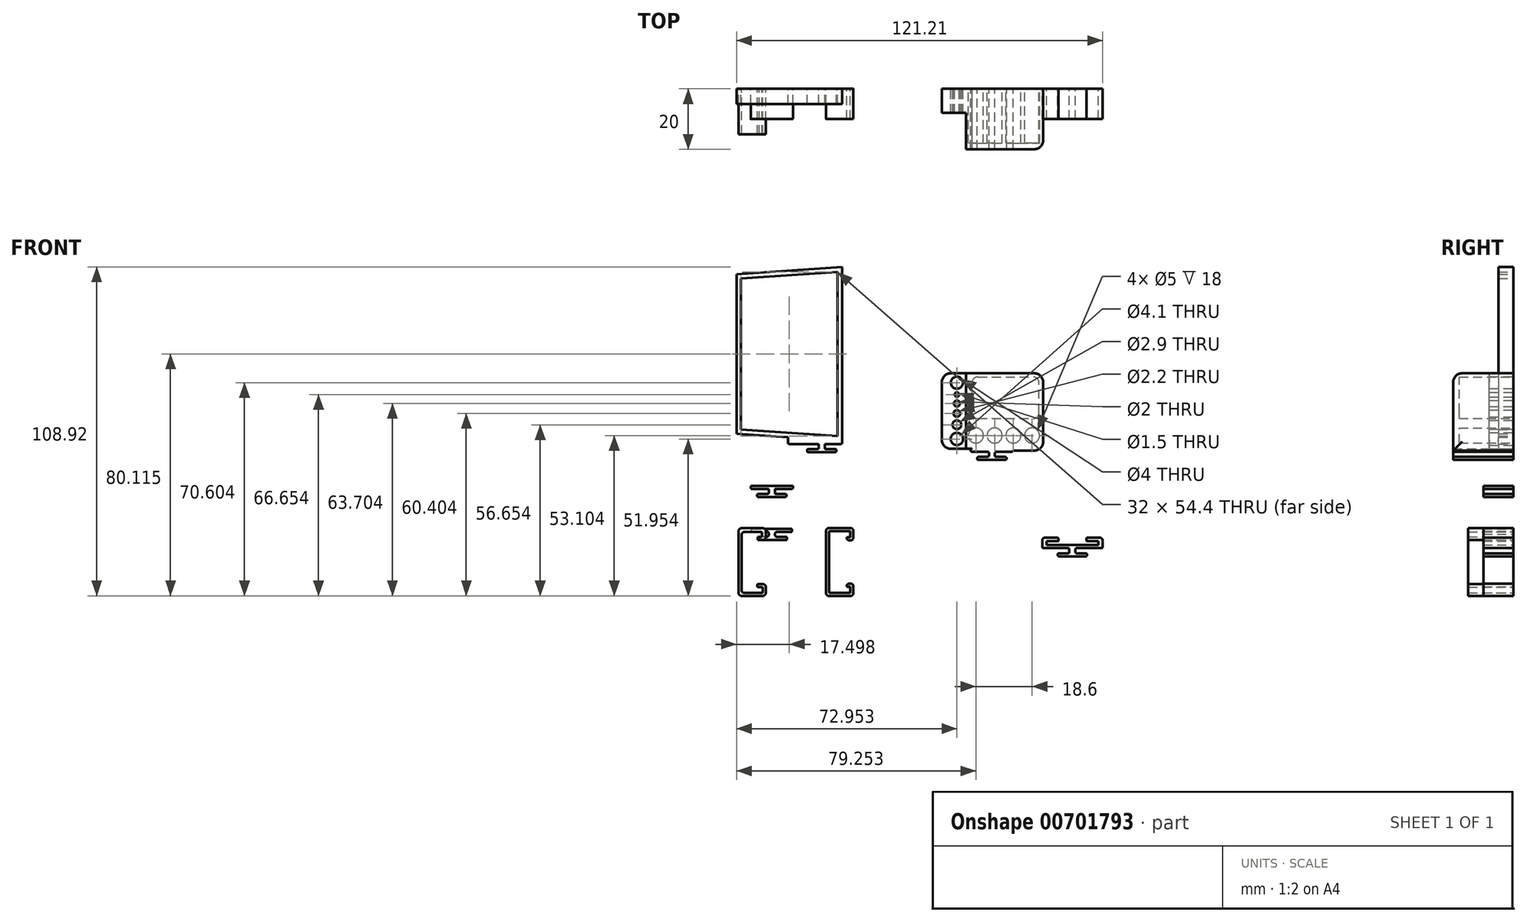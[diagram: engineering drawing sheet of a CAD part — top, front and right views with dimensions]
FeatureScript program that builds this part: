
annotation { "Feature Type Name" : "Feature", "Feature Type Description" : "" }
export const myFeature = defineFeature(function(context is Context, id is Id, definition is map)
    precondition{}
    {
        {
            var Q0;
            Q0=qCreatedBy(makeId("Front.planeOp"),FACE);
            var sketch = newSketch(context, id + "F0", { "sketchPlane" : qUnion([Q0])});
            skLineSegment(sketch, "E0.bottom", {"start": v(-9, 10) * mm, "end": v(-3.2, 10) * mm});
            skLineSegment(sketch, "E0.top", {"start": v(-9, -10) * mm, "end": v(-3.2, -10) * mm});
            skLineSegment(sketch, "E0.left", {"start": v(-10, 9) * mm, "end": v(-10, -9) * mm});
            skLineSegment(sketch, "E0.right", {"start": v(10, 9) * mm, "end": v(10, -9) * mm});
            skLineSegment(sketch, "E1.bottom", {"start": v(-3, 3) * mm, "end": v(3, 3) * mm});
            skLineSegment(sketch, "E1.top", {"start": v(-3, -3) * mm, "end": v(3, -3) * mm});
            skLineSegment(sketch, "E1.left", {"start": v(-3, 3) * mm, "end": v(-3, -3) * mm});
            skLineSegment(sketch, "E1.right", {"start": v(3, 3) * mm, "end": v(3, -3) * mm});
            skLineSegment(sketch, "E2", {"start": v(-3.2, 10) * mm, "end": v(-3.2, 8) * mm});
            skLineSegment(sketch, "E3", {"start": v(-3.2, 8) * mm, "end": v(-5.25, 8) * mm});
            skLineSegment(sketch, "E4", {"start": v(-5.25, 8) * mm, "end": v(-5.25, 6.5) * mm});
            skLineSegment(sketch, "E5", {"start": v(-5.25, 6.5) * mm, "end": v(-2.23, 3) * mm});
            skLineSegment(sketch, "E6", {"start": v(-3.2, -10) * mm, "end": v(-3.2, -8) * mm});
            skLineSegment(sketch, "E7", {"start": v(-3.2, -8) * mm, "end": v(-5.25, -8) * mm});
            skLineSegment(sketch, "E8", {"start": v(-5.25, -8) * mm, "end": v(-5.25, -6.5) * mm});
            skLineSegment(sketch, "E9", {"start": v(-5.25, -6.5) * mm, "end": v(-2.23, -3) * mm});
            skPoint(sketch, "E10.visualSharp", {"position": v(-10, 10) * mm});
            skArc(sketch, "E10.filletArc", {"start": v(-9, 10) * mm, "mid": v(-9.7, 9.7) * mm, "end": v(-10, 9) * mm});
            skPoint(sketch, "E11.visualSharp", {"position": v(-10, -10) * mm});
            skArc(sketch, "E11.filletArc", {"start": v(-10, -9) * mm, "mid": v(-9.7, -9.7) * mm, "end": v(-9, -10) * mm});
            skPoint(sketch, "E12.visualSharp", {"position": v(10, -10) * mm});
            skArc(sketch, "E12.filletArc", {"start": v(9, -10) * mm, "mid": v(9.7, -9.7) * mm, "end": v(10, -9) * mm});
            skPoint(sketch, "E13.visualSharp", {"position": v(10, 10) * mm});
            skArc(sketch, "E13.filletArc", {"start": v(10, 9) * mm, "mid": v(9.7, 9.7) * mm, "end": v(9, 10) * mm});
            skLineSegment(sketch, "E14", {"start": v(-4.2, 8.3) * mm, "end": v(-3.3, 8.3) * mm});
            skLineSegment(sketch, "E15", {"start": v(-3, 8.6) * mm, "end": v(-3, 9.9) * mm});
            skLineSegment(sketch, "E16", {"start": v(-3.3, 10.2) * mm, "end": v(-9.2, 10.2) * mm});
            skLineSegment(sketch, "E17", {"start": v(-10, 9.4) * mm, "end": v(-10, -9.4) * mm});
            skLineSegment(sketch, "E18", {"start": v(-9.2, -10.2) * mm, "end": v(-3.3, -10.2) * mm});
            skLineSegment(sketch, "E19", {"start": v(-3, -9.9) * mm, "end": v(-3, -8.6) * mm});
            skLineSegment(sketch, "E20", {"start": v(-3.3, -8.3) * mm, "end": v(-4.74, -8.3) * mm});
            skLineSegment(sketch, "E21", {"start": v(-4.74, -8.3) * mm, "end": v(-4.74, -7.6) * mm});
            skLineSegment(sketch, "E22", {"start": v(-4.44, -7.3) * mm, "end": v(-3, -7.3) * mm});
            skLineSegment(sketch, "E23", {"start": v(-2, -8.3) * mm, "end": v(-2, -10.2) * mm});
            skLineSegment(sketch, "E24", {"start": v(-3, -11.2) * mm, "end": v(-10, -11.2) * mm});
            skLineSegment(sketch, "E25", {"start": v(-11, -10.2) * mm, "end": v(-11, 10.2) * mm});
            skLineSegment(sketch, "E26", {"start": v(-10, 11.2) * mm, "end": v(-3, 11.2) * mm});
            skLineSegment(sketch, "E27", {"start": v(-2, 10.2) * mm, "end": v(-2, 8.3) * mm});
            skLineSegment(sketch, "E28", {"start": v(-3, 7.3) * mm, "end": v(-3.9, 7.3) * mm});
            skLineSegment(sketch, "E29", {"start": v(-4.2, 7.6) * mm, "end": v(-4.2, 8.3) * mm});
            skLineSegment(sketch, "E30.trimOffspring", {"start": v(-2, -10) * mm, "end": v(9, -10) * mm});
            skPoint(sketch, "E31.visualSharp", {"position": v(-11, -11.2) * mm});
            skArc(sketch, "E31.filletArc", {"start": v(-11, -10.2) * mm, "mid": v(-10.7, -10.9) * mm, "end": v(-10, -11.2) * mm});
            skPoint(sketch, "E32.visualSharp", {"position": v(-2, -11.2) * mm});
            skArc(sketch, "E32.filletArc", {"start": v(-3, -11.2) * mm, "mid": v(-2.3, -10.9) * mm, "end": v(-2, -10.2) * mm});
            skPoint(sketch, "E33.visualSharp", {"position": v(-11, 11.2) * mm});
            skArc(sketch, "E33.filletArc", {"start": v(-10, 11.2) * mm, "mid": v(-10.7, 10.9) * mm, "end": v(-11, 10.2) * mm});
            skPoint(sketch, "E34.visualSharp", {"position": v(-2, 11.2) * mm});
            skArc(sketch, "E34.filletArc", {"start": v(-2, 10.2) * mm, "mid": v(-2.3, 10.9) * mm, "end": v(-3, 11.2) * mm});
            skPoint(sketch, "E35.visualSharp", {"position": v(-2, -7.3) * mm});
            skArc(sketch, "E35.filletArc", {"start": v(-2, -8.3) * mm, "mid": v(-2.3, -7.6) * mm, "end": v(-3, -7.3) * mm});
            skPoint(sketch, "E36.visualSharp", {"position": v(-2, 7.3) * mm});
            skArc(sketch, "E36.filletArc", {"start": v(-3, 7.3) * mm, "mid": v(-2.3, 7.6) * mm, "end": v(-2, 8.3) * mm});
            skPoint(sketch, "E37.visualSharp", {"position": v(-4.2, 7.3) * mm});
            skArc(sketch, "E37.filletArc", {"start": v(-4.2, 7.6) * mm, "mid": v(-4.11, 7.39) * mm, "end": v(-3.9, 7.3) * mm});
            skPoint(sketch, "E38.visualSharp", {"position": v(-4.74, -7.3) * mm});
            skArc(sketch, "E38.filletArc", {"start": v(-4.44, -7.3) * mm, "mid": v(-4.65, -7.39) * mm, "end": v(-4.74, -7.6) * mm});
            skArc(sketch, "E39.filletArc", {"start": v(-3.3, 8.3) * mm, "mid": v(-3.09, 8.39) * mm, "end": v(-3, 8.6) * mm});
            skArc(sketch, "E40.filletArc", {"start": v(-3, 9.9) * mm, "mid": v(-3.09, 10.11) * mm, "end": v(-3.3, 10.2) * mm});
            skArc(sketch, "E41.filletArc", {"start": v(-3, -8.6) * mm, "mid": v(-3.09, -8.39) * mm, "end": v(-3.3, -8.3) * mm});
            skArc(sketch, "E42.filletArc", {"start": v(-3.3, -10.2) * mm, "mid": v(-3.09, -10.11) * mm, "end": v(-3, -9.9) * mm});
            skArc(sketch, "E43.filletArc", {"start": v(-10, -9.4) * mm, "mid": v(-9.77, -9.97) * mm, "end": v(-9.2, -10.2) * mm});
            skArc(sketch, "E44.filletArc", {"start": v(-9.2, 10.2) * mm, "mid": v(-9.77, 9.97) * mm, "end": v(-10, 9.4) * mm});
            skLineSegment(sketch, "E45", {"start": v(3.2, 10) * mm, "end": v(3.2, 8) * mm});
            skLineSegment(sketch, "E46", {"start": v(3.2, 8) * mm, "end": v(5.25, 8) * mm});
            skLineSegment(sketch, "E47", {"start": v(5.25, 8) * mm, "end": v(5.25, 6.5) * mm});
            skLineSegment(sketch, "E48", {"start": v(5.25, 6.5) * mm, "end": v(2.23, 3) * mm});
            skLineSegment(sketch, "E49.bottom", {"start": v(1.8, 8.3) * mm, "end": v(4.5, 8.3) * mm});
            skLineSegment(sketch, "E49.top", {"start": v(-3.2, 7.3) * mm, "end": v(5.3, 7.3) * mm});
            skLineSegment(sketch, "E49.left", {"start": v(-3.2, 8.8) * mm, "end": v(-3.2, 7.3) * mm});
            skLineSegment(sketch, "E50.top", {"start": v(-4.64, 11) * mm, "end": v(4.5, 11) * mm});
            skLineSegment(sketch, "E51.top", {"start": v(-0.8, 8.3) * mm, "end": v(1, 8.3) * mm});
            skArc(sketch, "E52.filletArc", {"start": v(1, 9.15) * mm, "mid": v(1.22, 8.55) * mm, "end": v(1.8, 8.3) * mm});
            skLineSegment(sketch, "E53", {"start": v(-1.8, 8.3) * mm, "end": v(-4.2, 8.3) * mm});
            skPoint(sketch, "E54.visualSharp", {"position": v(-0.8, 8.3) * mm});
            skArc(sketch, "E54.filletArc", {"start": v(-1.8, 8.3) * mm, "mid": v(-1.22, 8.55) * mm, "end": v(-1, 9.15) * mm});
            skPoint(sketch, "E55.visualSharp", {"position": v(-0.8, 10.05) * mm});
            skLineSegment(sketch, "E56.bottom", {"start": v(-4.2, 8.3) * mm, "end": v(-4.7, 8.3) * mm});
            skLineSegment(sketch, "E56.top", {"start": v(-4.2, 7.3) * mm, "end": v(-4.7, 7.3) * mm});
            skLineSegment(sketch, "E56.left", {"start": v(-4.2, 8) * mm, "end": v(-4.2, 7.3) * mm});
            skLineSegment(sketch, "E56.right", {"start": v(-4.7, 8.3) * mm, "end": v(-4.7, 7.3) * mm});
            skLineSegment(sketch, "E57", {"start": v(-3.2, 7.3) * mm, "end": v(-4.7, 7.3) * mm});
            skLineSegment(sketch, "E58", {"start": v(-4.7, 7.3) * mm, "end": v(-2, 7.3) * mm});
            skLineSegment(sketch, "E59.bottom", {"start": v(4.5, 8.3) * mm, "end": v(5, 8.3) * mm});
            skLineSegment(sketch, "E59.top", {"start": v(5, 7.3) * mm, "end": v(5.3, 7.3) * mm});
            skLineSegment(sketch, "E59.right", {"start": v(5, 8.3) * mm, "end": v(5, 7.3) * mm});
            skLineSegment(sketch, "E60.right", {"start": v(6.64, 10) * mm, "end": v(6.64, 11) * mm});
            skLineSegment(sketch, "E61.bottom", {"start": v(-4.64, 11) * mm, "end": v(-6.64, 11) * mm});
            skLineSegment(sketch, "E61.top", {"start": v(-4.5, 10.2) * mm, "end": v(-6.64, 10.2) * mm});
            skLineSegment(sketch, "E61.right", {"start": v(-6.64, 10.2) * mm, "end": v(-6.64, 11) * mm});
            skLineSegment(sketch, "E62", {"start": v(-1, 9.15) * mm, "end": v(-1, 9.15) * mm});
            skLineSegment(sketch, "E63", {"start": v(4.5, 11) * mm, "end": v(6.64, 11) * mm});
            skLineSegment(sketch, "E64", {"start": v(1, 9.15) * mm, "end": v(1, 9.2) * mm});
            skLineSegment(sketch, "E65", {"start": v(1.8, 10) * mm, "end": v(6.64, 10) * mm});
            skLineSegment(sketch, "E66", {"start": v(6.64, 10) * mm, "end": v(9, 10) * mm});
            skPoint(sketch, "E67.visualSharp", {"position": v(1, 10) * mm});
            skArc(sketch, "E67.filletArc", {"start": v(1.8, 10) * mm, "mid": v(1.23, 9.77) * mm, "end": v(1, 9.2) * mm});
            skLineSegment(sketch, "E68", {"start": v(-3.3, 10.2) * mm, "end": v(-1.8, 10.2) * mm});
            skLineSegment(sketch, "E69", {"start": v(-1, 9.4) * mm, "end": v(-1, 9.15) * mm});
            skPoint(sketch, "E70.visualSharp", {"position": v(-1, 10.2) * mm});
            skArc(sketch, "E70.filletArc", {"start": v(-1, 9.4) * mm, "mid": v(-1.23, 9.97) * mm, "end": v(-1.8, 10.2) * mm});
            skLineSegment(sketch, "E71", {"start": v(24.8, 8.2) * mm, "end": v(24.8, 8) * mm});
            skLineSegment(sketch, "E72", {"start": v(25.6, 7.2) * mm, "end": v(26.2, 7.2) * mm});
            skLineSegment(sketch, "E73", {"start": v(27, 8) * mm, "end": v(27, 10.4) * mm});
            skLineSegment(sketch, "E74", {"start": v(26.2, 11.2) * mm, "end": v(18.8, 11.2) * mm});
            skLineSegment(sketch, "E75", {"start": v(18, 10.4) * mm, "end": v(18, -10.4) * mm});
            skLineSegment(sketch, "E76", {"start": v(18.8, -11.2) * mm, "end": v(26.2, -11.2) * mm});
            skLineSegment(sketch, "E77", {"start": v(27, -10.4) * mm, "end": v(27, -8) * mm});
            skLineSegment(sketch, "E78", {"start": v(26.2, -7.2) * mm, "end": v(25.6, -7.2) * mm});
            skLineSegment(sketch, "E79", {"start": v(24.8, -8) * mm, "end": v(24.8, -8.2) * mm});
            skLineSegment(sketch, "E80", {"start": v(24.8, -8.2) * mm, "end": v(25.8, -8.2) * mm});
            skLineSegment(sketch, "E81", {"start": v(26, -8.4) * mm, "end": v(26, -10) * mm});
            skLineSegment(sketch, "E82", {"start": v(25.8, -10.2) * mm, "end": v(19.2, -10.2) * mm});
            skLineSegment(sketch, "E83", {"start": v(19, -10) * mm, "end": v(19, 10) * mm});
            skLineSegment(sketch, "E84", {"start": v(19.2, 10.2) * mm, "end": v(25.8, 10.2) * mm});
            skLineSegment(sketch, "E85", {"start": v(26, 10) * mm, "end": v(26, 8.4) * mm});
            skLineSegment(sketch, "E86", {"start": v(25.8, 8.2) * mm, "end": v(24.8, 8.2) * mm});
            skPoint(sketch, "E87.visualSharp", {"position": v(18, 11.2) * mm});
            skArc(sketch, "E87.filletArc", {"start": v(18.8, 11.2) * mm, "mid": v(18.23, 10.97) * mm, "end": v(18, 10.4) * mm});
            skPoint(sketch, "E88.visualSharp", {"position": v(27, 11.2) * mm});
            skArc(sketch, "E88.filletArc", {"start": v(27, 10.4) * mm, "mid": v(26.77, 10.97) * mm, "end": v(26.2, 11.2) * mm});
            skPoint(sketch, "E89.visualSharp", {"position": v(27, 7.2) * mm});
            skArc(sketch, "E89.filletArc", {"start": v(26.2, 7.2) * mm, "mid": v(26.77, 7.43) * mm, "end": v(27, 8) * mm});
            skPoint(sketch, "E90.visualSharp", {"position": v(24.8, 7.2) * mm});
            skArc(sketch, "E90.filletArc", {"start": v(24.8, 8) * mm, "mid": v(25.03, 7.43) * mm, "end": v(25.6, 7.2) * mm});
            skPoint(sketch, "E91.visualSharp", {"position": v(24.8, -7.2) * mm});
            skArc(sketch, "E91.filletArc", {"start": v(25.6, -7.2) * mm, "mid": v(25.03, -7.43) * mm, "end": v(24.8, -8) * mm});
            skPoint(sketch, "E92.visualSharp", {"position": v(27, -7.2) * mm});
            skArc(sketch, "E92.filletArc", {"start": v(27, -8) * mm, "mid": v(26.77, -7.43) * mm, "end": v(26.2, -7.2) * mm});
            skPoint(sketch, "E93.visualSharp", {"position": v(27, -11.2) * mm});
            skArc(sketch, "E93.filletArc", {"start": v(26.2, -11.2) * mm, "mid": v(26.77, -10.97) * mm, "end": v(27, -10.4) * mm});
            skPoint(sketch, "E94.visualSharp", {"position": v(18, -11.2) * mm});
            skArc(sketch, "E94.filletArc", {"start": v(18, -10.4) * mm, "mid": v(18.23, -10.97) * mm, "end": v(18.8, -11.2) * mm});
            skPoint(sketch, "E95.visualSharp", {"position": v(19, -10.2) * mm});
            skArc(sketch, "E95.filletArc", {"start": v(19, -10) * mm, "mid": v(19.06, -10.14) * mm, "end": v(19.2, -10.2) * mm});
            skPoint(sketch, "E96.visualSharp", {"position": v(26, -10.2) * mm});
            skArc(sketch, "E96.filletArc", {"start": v(25.8, -10.2) * mm, "mid": v(25.94, -10.14) * mm, "end": v(26, -10) * mm});
            skPoint(sketch, "E97.visualSharp", {"position": v(26, -8.2) * mm});
            skArc(sketch, "E97.filletArc", {"start": v(26, -8.4) * mm, "mid": v(25.94, -8.26) * mm, "end": v(25.8, -8.2) * mm});
            skPoint(sketch, "E98.visualSharp", {"position": v(19, 10.2) * mm});
            skArc(sketch, "E98.filletArc", {"start": v(19.2, 10.2) * mm, "mid": v(19.06, 10.14) * mm, "end": v(19, 10) * mm});
            skPoint(sketch, "E99.visualSharp", {"position": v(26, 10.2) * mm});
            skArc(sketch, "E99.filletArc", {"start": v(26, 10) * mm, "mid": v(25.94, 10.14) * mm, "end": v(25.8, 10.2) * mm});
            skPoint(sketch, "E100.visualSharp", {"position": v(26, 8.2) * mm});
            skArc(sketch, "E100.filletArc", {"start": v(25.8, 8.2) * mm, "mid": v(25.94, 8.26) * mm, "end": v(26, 8.4) * mm});
            skLineSegment(sketch, "E101", {"start": v(-6.6, 25.24) * mm, "end": v(7, 25.24) * mm});
            skLineSegment(sketch, "E102", {"start": v(7, 25.24) * mm, "end": v(7, 24.64) * mm});
            skLineSegment(sketch, "E103", {"start": v(6.6, 24.24) * mm, "end": v(1.4, 24.24) * mm});
            skLineSegment(sketch, "E104", {"start": v(1, 23.84) * mm, "end": v(1, 22.94) * mm});
            skLineSegment(sketch, "E105", {"start": v(1.4, 22.54) * mm, "end": v(4.45, 22.54) * mm});
            skLineSegment(sketch, "E106", {"start": v(4.85, 22.14) * mm, "end": v(4.85, 21.94) * mm});
            skLineSegment(sketch, "E107", {"start": v(4.45, 21.54) * mm, "end": v(-4.45, 21.54) * mm});
            skLineSegment(sketch, "E108", {"start": v(-4.85, 21.94) * mm, "end": v(-4.85, 22.14) * mm});
            skLineSegment(sketch, "E109", {"start": v(-4.45, 22.54) * mm, "end": v(-1.4, 22.54) * mm});
            skLineSegment(sketch, "E110", {"start": v(-1, 22.94) * mm, "end": v(-1, 23.84) * mm});
            skLineSegment(sketch, "E111", {"start": v(-1.4, 24.24) * mm, "end": v(-6.6, 24.24) * mm});
            skLineSegment(sketch, "E112", {"start": v(-7, 24.64) * mm, "end": v(-7, 24.84) * mm});
            skPoint(sketch, "E113.visualSharp", {"position": v(-1, 22.54) * mm});
            skArc(sketch, "E113.filletArc", {"start": v(-1.4, 22.54) * mm, "mid": v(-1.12, 22.66) * mm, "end": v(-1, 22.94) * mm});
            skPoint(sketch, "E114.visualSharp", {"position": v(1, 22.54) * mm});
            skArc(sketch, "E114.filletArc", {"start": v(1, 22.94) * mm, "mid": v(1.12, 22.66) * mm, "end": v(1.4, 22.54) * mm});
            skPoint(sketch, "E115.visualSharp", {"position": v(1, 24.24) * mm});
            skArc(sketch, "E115.filletArc", {"start": v(1.4, 24.24) * mm, "mid": v(1.12, 24.13) * mm, "end": v(1, 23.84) * mm});
            skPoint(sketch, "E116.visualSharp", {"position": v(-1, 24.24) * mm});
            skArc(sketch, "E116.filletArc", {"start": v(-1, 23.84) * mm, "mid": v(-1.12, 24.13) * mm, "end": v(-1.4, 24.24) * mm});
            skPoint(sketch, "E117.visualSharp", {"position": v(-4.85, 22.54) * mm});
            skArc(sketch, "E117.filletArc", {"start": v(-4.45, 22.54) * mm, "mid": v(-4.73, 22.43) * mm, "end": v(-4.85, 22.14) * mm});
            skPoint(sketch, "E118.visualSharp", {"position": v(-4.85, 21.54) * mm});
            skArc(sketch, "E118.filletArc", {"start": v(-4.85, 21.94) * mm, "mid": v(-4.73, 21.66) * mm, "end": v(-4.45, 21.54) * mm});
            skPoint(sketch, "E119.visualSharp", {"position": v(4.85, 21.54) * mm});
            skArc(sketch, "E119.filletArc", {"start": v(4.45, 21.54) * mm, "mid": v(4.73, 21.66) * mm, "end": v(4.85, 21.94) * mm});
            skPoint(sketch, "E120.visualSharp", {"position": v(4.85, 22.54) * mm});
            skArc(sketch, "E120.filletArc", {"start": v(4.85, 22.14) * mm, "mid": v(4.73, 22.43) * mm, "end": v(4.45, 22.54) * mm});
            skPoint(sketch, "E121.visualSharp", {"position": v(7, 24.24) * mm});
            skArc(sketch, "E121.filletArc", {"start": v(6.6, 24.24) * mm, "mid": v(6.88, 24.36) * mm, "end": v(7, 24.64) * mm});
            skPoint(sketch, "E122.visualSharp", {"position": v(-7, 25.24) * mm});
            skArc(sketch, "E122.filletArc", {"start": v(-6.6, 25.24) * mm, "mid": v(-6.88, 25.13) * mm, "end": v(-7, 24.84) * mm});
            skPoint(sketch, "E123.visualSharp", {"position": v(-7, 24.24) * mm});
            skArc(sketch, "E123.filletArc", {"start": v(-7, 24.64) * mm, "mid": v(-6.88, 24.36) * mm, "end": v(-6.6, 24.24) * mm});
            skLineSegment(sketch, "E124", {"start": v(21.82, 96.11) * mm, "end": v(21.82, 41.71) * mm});
            skLineSegment(sketch, "E125", {"start": v(21.82, 96.11) * mm, "end": v(-10.18, 93.96) * mm});
            skLineSegment(sketch, "E126", {"start": v(-10.18, 93.96) * mm, "end": v(-10.18, 43.86) * mm});
            skLineSegment(sketch, "E127", {"start": v(-10.18, 43.86) * mm, "end": v(21.82, 41.71) * mm});
            skLineSegment(sketch, "E128", {"start": v(13.05, 68.91) * mm, "end": v(-2.86, 68.91) * mm, "construction": true});
            skPoint(sketch, "E128.startSnap0", {"position": v(21.82, 68.91) * mm});
            skLineSegment(sketch, "E129.0", {"start": v(-11.68, 42.46) * mm, "end": v(5.32, 41.32) * mm});
            skLineSegment(sketch, "E129.1", {"start": v(-11.68, 95.37) * mm, "end": v(-11.68, 42.46) * mm});
            skLineSegment(sketch, "E129.2", {"start": v(23.32, 97.72) * mm, "end": v(-11.68, 95.37) * mm});
            skLineSegment(sketch, "E129.3", {"start": v(23.32, 97.72) * mm, "end": v(23.32, 40.11) * mm});
            skLineSegment(sketch, "E130", {"start": v(23.32, 40.11) * mm, "end": v(23.32, 39.51) * mm});
            skLineSegment(sketch, "E131", {"start": v(22.92, 39.11) * mm, "end": v(17.92, 39.11) * mm});
            skLineSegment(sketch, "E132", {"start": v(17.52, 38.71) * mm, "end": v(17.52, 37.81) * mm});
            skLineSegment(sketch, "E133", {"start": v(17.92, 37.41) * mm, "end": v(20.97, 37.41) * mm});
            skLineSegment(sketch, "E134", {"start": v(21.37, 37.01) * mm, "end": v(21.37, 36.81) * mm});
            skLineSegment(sketch, "E135", {"start": v(20.97, 36.41) * mm, "end": v(12.07, 36.41) * mm});
            skLineSegment(sketch, "E136", {"start": v(11.67, 36.81) * mm, "end": v(11.67, 37.01) * mm});
            skLineSegment(sketch, "E137", {"start": v(12.07, 37.41) * mm, "end": v(15.12, 37.41) * mm});
            skLineSegment(sketch, "E138", {"start": v(15.52, 37.81) * mm, "end": v(15.52, 38.71) * mm});
            skLineSegment(sketch, "E139", {"start": v(15.12, 39.11) * mm, "end": v(5.72, 39.11) * mm});
            skLineSegment(sketch, "E140", {"start": v(5.32, 39.51) * mm, "end": v(5.32, 39.71) * mm});
            skPoint(sketch, "E141.visualSharp", {"position": v(15.52, 37.41) * mm});
            skArc(sketch, "E141.filletArc", {"start": v(15.12, 37.41) * mm, "mid": v(15.4, 37.53) * mm, "end": v(15.52, 37.81) * mm});
            skPoint(sketch, "E142.visualSharp", {"position": v(17.52, 37.41) * mm});
            skArc(sketch, "E142.filletArc", {"start": v(17.52, 37.81) * mm, "mid": v(17.64, 37.53) * mm, "end": v(17.92, 37.41) * mm});
            skPoint(sketch, "E143.visualSharp", {"position": v(17.52, 39.11) * mm});
            skArc(sketch, "E143.filletArc", {"start": v(17.92, 39.11) * mm, "mid": v(17.64, 39) * mm, "end": v(17.52, 38.71) * mm});
            skPoint(sketch, "E144.visualSharp", {"position": v(15.52, 39.11) * mm});
            skArc(sketch, "E144.filletArc", {"start": v(15.52, 38.71) * mm, "mid": v(15.4, 39) * mm, "end": v(15.12, 39.11) * mm});
            skPoint(sketch, "E145.visualSharp", {"position": v(11.67, 37.41) * mm});
            skArc(sketch, "E145.filletArc", {"start": v(12.07, 37.41) * mm, "mid": v(11.79, 37.3) * mm, "end": v(11.67, 37.01) * mm});
            skPoint(sketch, "E146.visualSharp", {"position": v(11.67, 36.41) * mm});
            skArc(sketch, "E146.filletArc", {"start": v(11.67, 36.81) * mm, "mid": v(11.79, 36.53) * mm, "end": v(12.07, 36.41) * mm});
            skPoint(sketch, "E147.visualSharp", {"position": v(21.37, 36.41) * mm});
            skArc(sketch, "E147.filletArc", {"start": v(20.97, 36.41) * mm, "mid": v(21.25, 36.53) * mm, "end": v(21.37, 36.81) * mm});
            skPoint(sketch, "E148.visualSharp", {"position": v(21.37, 37.41) * mm});
            skArc(sketch, "E148.filletArc", {"start": v(21.37, 37.01) * mm, "mid": v(21.25, 37.3) * mm, "end": v(20.97, 37.41) * mm});
            skPoint(sketch, "E149.visualSharp", {"position": v(23.32, 39.11) * mm});
            skArc(sketch, "E149.filletArc", {"start": v(22.92, 39.11) * mm, "mid": v(23.2, 39.23) * mm, "end": v(23.32, 39.51) * mm});
            skPoint(sketch, "E150.visualSharp", {"position": v(5.32, 40.11) * mm});
            skPoint(sketch, "E151.visualSharp", {"position": v(5.32, 39.11) * mm});
            skArc(sketch, "E151.filletArc", {"start": v(5.32, 39.51) * mm, "mid": v(5.44, 39.23) * mm, "end": v(5.72, 39.11) * mm});
            skLineSegment(sketch, "E152", {"start": v(16.52, 42.74) * mm, "end": v(16.52, 31.82) * mm, "construction": true});
            skPoint(sketch, "E152.startSnap0", {"position": v(16.52, 40.11) * mm});
            skLineSegment(sketch, "E153", {"start": v(5.32, 39.71) * mm, "end": v(5.32, 41.32) * mm});
            skLineSegment(sketch, "E154", {"start": v(66.27, 37.5) * mm, "end": v(79.87, 37.5) * mm});
            skLineSegment(sketch, "E155", {"start": v(79.87, 37.5) * mm, "end": v(79.87, 36.9) * mm});
            skLineSegment(sketch, "E156", {"start": v(79.47, 36.5) * mm, "end": v(74.27, 36.5) * mm});
            skLineSegment(sketch, "E157", {"start": v(73.87, 36.1) * mm, "end": v(73.87, 35.2) * mm});
            skLineSegment(sketch, "E158", {"start": v(74.27, 34.8) * mm, "end": v(77.32, 34.8) * mm});
            skLineSegment(sketch, "E159", {"start": v(77.72, 34.4) * mm, "end": v(77.72, 34.2) * mm});
            skLineSegment(sketch, "E160", {"start": v(77.32, 33.8) * mm, "end": v(68.42, 33.8) * mm});
            skLineSegment(sketch, "E161", {"start": v(68.02, 34.2) * mm, "end": v(68.02, 34.4) * mm});
            skLineSegment(sketch, "E162", {"start": v(68.42, 34.8) * mm, "end": v(71.47, 34.8) * mm});
            skLineSegment(sketch, "E163", {"start": v(71.87, 35.2) * mm, "end": v(71.87, 36.1) * mm});
            skLineSegment(sketch, "E164", {"start": v(71.47, 36.5) * mm, "end": v(66.27, 36.5) * mm});
            skLineSegment(sketch, "E165", {"start": v(65.87, 36.9) * mm, "end": v(65.87, 37.1) * mm});
            skPoint(sketch, "E166.visualSharp", {"position": v(71.87, 34.8) * mm});
            skArc(sketch, "E166.filletArc", {"start": v(71.47, 34.8) * mm, "mid": v(71.76, 34.92) * mm, "end": v(71.87, 35.2) * mm});
            skPoint(sketch, "E167.visualSharp", {"position": v(73.87, 34.8) * mm});
            skArc(sketch, "E167.filletArc", {"start": v(73.87, 35.2) * mm, "mid": v(74, 34.92) * mm, "end": v(74.27, 34.8) * mm});
            skPoint(sketch, "E168.visualSharp", {"position": v(73.87, 36.5) * mm});
            skArc(sketch, "E168.filletArc", {"start": v(74.27, 36.5) * mm, "mid": v(74, 36.39) * mm, "end": v(73.87, 36.1) * mm});
            skPoint(sketch, "E169.visualSharp", {"position": v(71.87, 36.5) * mm});
            skArc(sketch, "E169.filletArc", {"start": v(71.87, 36.1) * mm, "mid": v(71.76, 36.39) * mm, "end": v(71.47, 36.5) * mm});
            skPoint(sketch, "E170.visualSharp", {"position": v(68.02, 34.8) * mm});
            skArc(sketch, "E170.filletArc", {"start": v(68.42, 34.8) * mm, "mid": v(68.14, 34.69) * mm, "end": v(68.02, 34.4) * mm});
            skPoint(sketch, "E171.visualSharp", {"position": v(68.02, 33.8) * mm});
            skArc(sketch, "E171.filletArc", {"start": v(68.02, 34.2) * mm, "mid": v(68.14, 33.92) * mm, "end": v(68.42, 33.8) * mm});
            skPoint(sketch, "E172.visualSharp", {"position": v(77.72, 33.8) * mm});
            skArc(sketch, "E172.filletArc", {"start": v(77.32, 33.8) * mm, "mid": v(77.6, 33.92) * mm, "end": v(77.72, 34.2) * mm});
            skPoint(sketch, "E173.visualSharp", {"position": v(77.72, 34.8) * mm});
            skArc(sketch, "E173.filletArc", {"start": v(77.72, 34.4) * mm, "mid": v(77.6, 34.69) * mm, "end": v(77.32, 34.8) * mm});
            skPoint(sketch, "E174.visualSharp", {"position": v(79.87, 36.5) * mm});
            skArc(sketch, "E174.filletArc", {"start": v(79.47, 36.5) * mm, "mid": v(79.76, 36.62) * mm, "end": v(79.87, 36.9) * mm});
            skPoint(sketch, "E175.visualSharp", {"position": v(65.87, 37.5) * mm});
            skArc(sketch, "E175.filletArc", {"start": v(66.27, 37.5) * mm, "mid": v(66, 37.39) * mm, "end": v(65.87, 37.1) * mm});
            skPoint(sketch, "E176.visualSharp", {"position": v(65.87, 36.5) * mm});
            skArc(sketch, "E176.filletArc", {"start": v(65.87, 36.9) * mm, "mid": v(66, 36.62) * mm, "end": v(66.27, 36.5) * mm});
            skLineSegment(sketch, "E177", {"start": v(89.53, 5.6) * mm, "end": v(109.53, 5.6) * mm});
            skLineSegment(sketch, "E178", {"start": v(109.53, 5.6) * mm, "end": v(109.53, 5) * mm});
            skLineSegment(sketch, "E179", {"start": v(109.13, 4.6) * mm, "end": v(100.93, 4.6) * mm});
            skLineSegment(sketch, "E180", {"start": v(100.53, 4.2) * mm, "end": v(100.53, 3.3) * mm});
            skLineSegment(sketch, "E181", {"start": v(100.93, 2.9) * mm, "end": v(103.98, 2.9) * mm});
            skLineSegment(sketch, "E182", {"start": v(104.38, 2.5) * mm, "end": v(104.38, 2.3) * mm});
            skLineSegment(sketch, "E183", {"start": v(103.98, 1.9) * mm, "end": v(95.08, 1.9) * mm});
            skLineSegment(sketch, "E184", {"start": v(94.68, 2.3) * mm, "end": v(94.68, 2.5) * mm});
            skLineSegment(sketch, "E185", {"start": v(95.08, 2.9) * mm, "end": v(98.13, 2.9) * mm});
            skLineSegment(sketch, "E186", {"start": v(98.53, 3.3) * mm, "end": v(98.53, 4.2) * mm});
            skLineSegment(sketch, "E187", {"start": v(98.13, 4.6) * mm, "end": v(89.93, 4.6) * mm});
            skLineSegment(sketch, "E188", {"start": v(89.53, 5) * mm, "end": v(89.53, 5.18) * mm});
            skPoint(sketch, "E189.visualSharp", {"position": v(98.53, 2.9) * mm});
            skArc(sketch, "E189.filletArc", {"start": v(98.13, 2.9) * mm, "mid": v(98.4, 3) * mm, "end": v(98.53, 3.3) * mm});
            skPoint(sketch, "E190.visualSharp", {"position": v(100.53, 2.9) * mm});
            skArc(sketch, "E190.filletArc", {"start": v(100.53, 3.3) * mm, "mid": v(100.64, 3) * mm, "end": v(100.93, 2.9) * mm});
            skPoint(sketch, "E191.visualSharp", {"position": v(100.53, 4.6) * mm});
            skArc(sketch, "E191.filletArc", {"start": v(100.93, 4.6) * mm, "mid": v(100.64, 4.48) * mm, "end": v(100.53, 4.2) * mm});
            skPoint(sketch, "E192.visualSharp", {"position": v(98.53, 4.6) * mm});
            skArc(sketch, "E192.filletArc", {"start": v(98.53, 4.2) * mm, "mid": v(98.4, 4.48) * mm, "end": v(98.13, 4.6) * mm});
            skPoint(sketch, "E193.visualSharp", {"position": v(94.68, 2.9) * mm});
            skArc(sketch, "E193.filletArc", {"start": v(95.08, 2.9) * mm, "mid": v(94.8, 2.78) * mm, "end": v(94.68, 2.5) * mm});
            skPoint(sketch, "E194.visualSharp", {"position": v(94.68, 1.9) * mm});
            skArc(sketch, "E194.filletArc", {"start": v(94.68, 2.3) * mm, "mid": v(94.8, 2) * mm, "end": v(95.08, 1.9) * mm});
            skPoint(sketch, "E195.visualSharp", {"position": v(104.38, 1.9) * mm});
            skArc(sketch, "E195.filletArc", {"start": v(103.98, 1.9) * mm, "mid": v(104.26, 2) * mm, "end": v(104.38, 2.3) * mm});
            skPoint(sketch, "E196.visualSharp", {"position": v(104.38, 2.9) * mm});
            skArc(sketch, "E196.filletArc", {"start": v(104.38, 2.5) * mm, "mid": v(104.26, 2.78) * mm, "end": v(103.98, 2.9) * mm});
            skPoint(sketch, "E197.visualSharp", {"position": v(109.53, 4.6) * mm});
            skArc(sketch, "E197.filletArc", {"start": v(109.13, 4.6) * mm, "mid": v(109.4, 4.7) * mm, "end": v(109.53, 5) * mm});
            skPoint(sketch, "E198.visualSharp", {"position": v(89.53, 4.6) * mm});
            skArc(sketch, "E198.filletArc", {"start": v(89.53, 5) * mm, "mid": v(89.64, 4.7) * mm, "end": v(89.93, 4.6) * mm});
            skPoint(sketch, "E199.startSnap0", {"position": v(99.53, 1.9) * mm});
            skLineSegment(sketch, "E200", {"start": v(89.53, 5.18) * mm, "end": v(89.53, 5.6) * mm});
            skLineSegment(sketch, "E201", {"start": v(99.53, -2.23) * mm, "end": v(99.53, 10.82) * mm, "construction": true});
            skLineSegment(sketch, "E202", {"start": v(109.53, 5.6) * mm, "end": v(109.53, 7.1) * mm});
            skLineSegment(sketch, "E203", {"start": v(108.53, 8.1) * mm, "end": v(104.63, 8.1) * mm});
            skLineSegment(sketch, "E204", {"start": v(104.13, 7.6) * mm, "end": v(104.13, 6.9) * mm});
            skLineSegment(sketch, "E205", {"start": v(104.13, 6.9) * mm, "end": v(108.13, 6.9) * mm});
            skLineSegment(sketch, "E206", {"start": v(108.13, 6.9) * mm, "end": v(108.13, 5.6) * mm});
            skLineSegment(sketch, "E207", {"start": v(89.53, 5.6) * mm, "end": v(89.53, 7.1) * mm});
            skLineSegment(sketch, "E208", {"start": v(90.53, 8.1) * mm, "end": v(94.43, 8.1) * mm});
            skLineSegment(sketch, "E209", {"start": v(94.93, 7.6) * mm, "end": v(94.93, 6.9) * mm});
            skLineSegment(sketch, "E210", {"start": v(94.93, 6.9) * mm, "end": v(90.93, 6.9) * mm});
            skLineSegment(sketch, "E211", {"start": v(90.93, 6.9) * mm, "end": v(90.93, 5.6) * mm});
            skPoint(sketch, "E212.visualSharp", {"position": v(109.53, 8.1) * mm});
            skArc(sketch, "E212.filletArc", {"start": v(109.53, 7.1) * mm, "mid": v(109.23, 7.8) * mm, "end": v(108.53, 8.1) * mm});
            skPoint(sketch, "E213.visualSharp", {"position": v(89.53, 8.1) * mm});
            skArc(sketch, "E213.filletArc", {"start": v(90.53, 8.1) * mm, "mid": v(89.82, 7.8) * mm, "end": v(89.53, 7.1) * mm});
            skPoint(sketch, "E214.visualSharp", {"position": v(94.93, 8.1) * mm});
            skArc(sketch, "E214.filletArc", {"start": v(94.93, 7.6) * mm, "mid": v(94.78, 7.95) * mm, "end": v(94.43, 8.1) * mm});
            skPoint(sketch, "E215.visualSharp", {"position": v(104.13, 8.1) * mm});
            skArc(sketch, "E215.filletArc", {"start": v(104.63, 8.1) * mm, "mid": v(104.27, 7.95) * mm, "end": v(104.13, 7.6) * mm});
            skSolve(sketch);
        }
        {
            var Q0;
            Q0=makeQuery(id+"F0.imprint","IMPRINT",FACE,{"disambiguationData":[TD([[makeQuery(id+"F0.imprint","IMPRINT",EDGE,{"derivedFrom":sQuery(id+"F0.wireOp",EDGE,"E14")}),-1.0]])]});
            var Q1;
            Q1=makeQuery(id+"F0.imprint","IMPRINT",FACE,{"disambiguationData":[TD([[makeQuery(id+"F0.imprint","IMPRINT",EDGE,{"derivedFrom":sQuery(id+"F0.wireOp",EDGE,"E16")}),-1.0]])]});
            var Q2;
            {var subQ0=sQuery(id+"F0.wireOp",EDGE,"E50.left");Q2=makeQuery(id+"F0.imprint","IMPRINT",FACE,{"disambiguationData":[TD([[makeQuery(id+"F0.imprint","IMPRINT",EDGE,{"derivedFrom":subQ0}),-1.0]])]});}
            var Q3;
            Q3=makeQuery(id+"F0.imprint","IMPRINT",FACE,{"disambiguationData":[TD([[makeQuery(id+"F0.imprint","IMPRINT",EDGE,{"derivedFrom":sQuery(id+"F0.wireOp",EDGE,"E15")}),-1.0]])]});
            var Q4;
            {var subQ0=sQuery(id+"F0.wireOp",EDGE,"E36.filletArc");var subQ1=sQuery(id+"F0.wireOp",EDGE,"E27");var subQ2=makeQuery(id+"F0.imprint","INTERSECT",VERTEX,{"derivedFrom":[subQ1,subQ0]});Q4=makeQuery(id+"F0.imprint","IMPRINT",FACE,{"disambiguationData":[TD([[makeQuery(id+"F0.imprint","IMPRINT",EDGE,{"disambiguationData":[TD([[subQ2,1.0]])],"derivedFrom":subQ1}),-1.0]])]});}
            var Q5;
            {var subQ0=sQuery(id+"F0.wireOp",EDGE,"E28");Q5=makeQuery(id+"F0.imprint","IMPRINT",FACE,{"disambiguationData":[TD([[makeQuery(id+"F0.imprint","IMPRINT",EDGE,{"derivedFrom":subQ0}),-1.0]])]});}
            var Q6;
            {var subQ5=sQuery(id+"F0.wireOp",EDGE,"E15");Q6=makeQuery(id+"F0.imprint","IMPRINT",FACE,{"disambiguationData":[TD([[makeQuery(id+"F0.imprint","IMPRINT",EDGE,{"derivedFrom":subQ5}),1.0]])]});}
            var Q7;
            {var subQ0=sQuery(id+"F0.wireOp",EDGE,"E49.left");var subQ1=sQuery(id+"F0.wireOp",EDGE,"E3");var subQ2=makeQuery(id+"F0.imprint","INTERSECT",VERTEX,{"derivedFrom":[subQ1,subQ0]});Q7=makeQuery(id+"F0.imprint","IMPRINT",FACE,{"disambiguationData":[TD([[makeQuery(id+"F0.imprint","IMPRINT",EDGE,{"disambiguationData":[TD([[subQ2,-1.0]])],"derivedFrom":subQ1}),-1.0]])]});}
            var Q8;
            {var subQ3=sQuery(id+"F0.wireOp",EDGE,"E36.filletArc");Q8=makeQuery(id+"F0.imprint","IMPRINT",FACE,{"disambiguationData":[TD([[makeQuery(id+"F0.imprint","IMPRINT",EDGE,{"derivedFrom":subQ3}),1.0]])]});}
            var Q9;
            {var subQ1=sQuery(id+"F0.wireOp",EDGE,"E20");Q9=makeQuery(id+"F0.imprint","IMPRINT",FACE,{"disambiguationData":[TD([[makeQuery(id+"F0.imprint","IMPRINT",EDGE,{"derivedFrom":subQ1}),-1.0]])]});}
            var Q10;
            {var subQ1=sQuery(id+"F0.wireOp",EDGE,"E37.filletArc");Q10=makeQuery(id+"F0.imprint","IMPRINT",FACE,{"disambiguationData":[TD([[makeQuery(id+"F0.imprint","IMPRINT",EDGE,{"derivedFrom":subQ1}),1.0]])]});}
            var Q11;
            {var subQ2=sQuery(id+"F0.wireOp",EDGE,"E61.top");Q11=makeQuery(id+"F0.imprint","IMPRINT",FACE,{"disambiguationData":[TD([[makeQuery(id+"F0.imprint","IMPRINT",EDGE,{"derivedFrom":subQ2}),-1.0]])]});}
            var Q12;
            {var subQ0=sQuery(id+"F0.wireOp",EDGE,"E34.filletArc");var subQ1=sQuery(id+"F0.wireOp",EDGE,"E26");var subQ2=makeQuery(id+"F0.imprint","INTERSECT",VERTEX,{"derivedFrom":[subQ1,subQ0]});Q12=makeQuery(id+"F0.imprint","IMPRINT",FACE,{"disambiguationData":[TD([[makeQuery(id+"F0.imprint","IMPRINT",EDGE,{"disambiguationData":[TD([[subQ2,1.0]])],"derivedFrom":subQ1}),-1.0]])]});}
            var Q13;
            {var subQ2=sQuery(id+"F0.wireOp",EDGE,"E34.filletArc");Q13=makeQuery(id+"F0.imprint","IMPRINT",FACE,{"disambiguationData":[TD([[makeQuery(id+"F0.imprint","IMPRINT",EDGE,{"derivedFrom":subQ2}),1.0]])]});}
            extrude(context, id + "F1", {"entities" : qUnion([Q0, Q1, Q2, Q3, Q4, Q5, Q6, Q7, Q8, Q9, Q10, Q11, Q12, Q13]), "depth" : 15 * mm, "offsetDistance" : 25 * mm});
        }
        {
            var Q0;
            {var subQ9=sQuery(id+"F0.wireOp",EDGE,"E50.bottom");Q0=makeQuery(id+"F0.imprint","IMPRINT",FACE,{"disambiguationData":[TD([[makeQuery(id+"F0.imprint","IMPRINT",EDGE,{"derivedFrom":subQ9}),1.0]])]});}
            var Q1;
            Q1=makeQuery(id+"F0.imprint","IMPRINT",FACE,{"disambiguationData":[TD([[makeQuery(id+"F0.imprint","IMPRINT",EDGE,{"derivedFrom":sQuery(id+"F0.wireOp",EDGE,"E60.bottom")}),-1.0]])]});
            var Q2;
            {var subQ17=sQuery(id+"F0.wireOp",EDGE,"E36.filletArc");Q2=makeQuery(id+"F0.imprint","IMPRINT",FACE,{"disambiguationData":[TD([[makeQuery(id+"F0.imprint","IMPRINT",EDGE,{"derivedFrom":subQ17}),-1.0]])]});}
            var Q3;
            {var subQ0=sQuery(id+"F0.wireOp",EDGE,"E34.filletArc");Q3=makeQuery(id+"F0.imprint","IMPRINT",FACE,{"disambiguationData":[TD([[makeQuery(id+"F0.imprint","IMPRINT",EDGE,{"derivedFrom":subQ0}),-1.0]])]});}
            var Q4;
            {var subQ1=sQuery(id+"F0.wireOp",EDGE,"E46");Q4=makeQuery(id+"F0.imprint","IMPRINT",FACE,{"disambiguationData":[TD([[makeQuery(id+"F0.imprint","IMPRINT",EDGE,{"derivedFrom":subQ1}),1.0]])]});}
            var Q5;
            {var subQ0=sQuery(id+"F0.wireOp",EDGE,"E36.filletArc");Q5=makeQuery(id+"F0.imprint","IMPRINT",FACE,{"disambiguationData":[TD([[makeQuery(id+"F0.imprint","IMPRINT",EDGE,{"derivedFrom":subQ0}),1.0]])]});}
            var Q6;
            {var subQ0=sQuery(id+"F0.wireOp",EDGE,"E29");Q6=makeQuery(id+"F0.imprint","IMPRINT",FACE,{"disambiguationData":[TD([[makeQuery(id+"F0.imprint","IMPRINT",EDGE,{"derivedFrom":subQ0}),-1.0]])]});}
            var Q7;
            {var subQ3=sQuery(id+"F0.wireOp",EDGE,"E37.filletArc");Q7=makeQuery(id+"F0.imprint","IMPRINT",FACE,{"disambiguationData":[TD([[makeQuery(id+"F0.imprint","IMPRINT",EDGE,{"derivedFrom":subQ3}),1.0]])]});}
            var Q8;
            {var subQ0=sQuery(id+"F0.wireOp",EDGE,"E29");Q8=makeQuery(id+"F0.imprint","IMPRINT",FACE,{"disambiguationData":[TD([[makeQuery(id+"F0.imprint","IMPRINT",EDGE,{"derivedFrom":subQ0}),1.0]])]});}
            var Q9;
            {var subQ0=sQuery(id+"F0.wireOp",EDGE,"E37.filletArc");Q9=makeQuery(id+"F0.imprint","IMPRINT",FACE,{"disambiguationData":[TD([[makeQuery(id+"F0.imprint","IMPRINT",EDGE,{"derivedFrom":subQ0}),-1.0]])]});}
            var Q10;
            {var subQ5=sQuery(id+"F0.wireOp",EDGE,"E56.left");var subQ6=makeQuery(id+"F0.imprint","INTERSECT",VERTEX,{"derivedFrom":[sQuery(id+"F0.wireOp",EDGE,"E37.filletArc"),subQ5]});Q10=makeQuery(id+"F0.imprint","IMPRINT",FACE,{"disambiguationData":[TD([[makeQuery(id+"F0.imprint","IMPRINT",EDGE,{"disambiguationData":[TD([[subQ6,-1.0]])],"derivedFrom":subQ5}),-1.0]])]});}
            var Q11;
            {var subQ0=sQuery(id+"F0.wireOp",EDGE,"E61.bottom");Q11=makeQuery(id+"F0.imprint","IMPRINT",FACE,{"disambiguationData":[TD([[makeQuery(id+"F0.imprint","IMPRINT",EDGE,{"derivedFrom":subQ0}),1.0]])]});}
            extrude(context, id + "F2", {"entities" : qUnion([Q0, Q1, Q2, Q3, Q4, Q5, Q6, Q7, Q8, Q9, Q10, Q11]), "depth" : 10 * mm, "offsetDistance" : 25 * mm});
        }
        {
            var Q0;
            Q0=makeQuery(id+"F0.imprint","IMPRINT",FACE,{"disambiguationData":[TD([[makeQuery(id+"F0.imprint","IMPRINT",EDGE,{"derivedFrom":sQuery(id+"F0.wireOp",EDGE,"E71")}),1.0]])]});
            extrude(context, id + "F3", {"entities" : qUnion([Q0]), "depth" : 10 * mm, "offsetDistance" : 25 * mm});
        }
        {
            var Q0;
            Q0=makeQuery(id+"F0.imprint","IMPRINT",FACE,{"disambiguationData":[TD([[makeQuery(id+"F0.imprint","IMPRINT",EDGE,{"derivedFrom":sQuery(id+"F0.wireOp",EDGE,"E101")}),-1.0]])]});
            extrude(context, id + "F4", {"entities" : qUnion([Q0]), "depth" : 10 * mm, "offsetDistance" : 25 * mm});
        }
        {
            var Q0;
            Q0=makeQuery(id+"F0.imprint","IMPRINT",FACE,{"disambiguationData":[TD([[makeQuery(id+"F0.imprint","IMPRINT",EDGE,{"derivedFrom":sQuery(id+"F0.wireOp",EDGE,"E124")}),1.0]])]});
            extrude(context, id + "F5", {"entities" : qUnion([Q0]), "depth" : 5 * mm, "offsetDistance" : 25 * mm});
        }
        {
            var Q0;
            Q0=makeQuery(id+"F0.imprint","IMPRINT",FACE,{"disambiguationData":[TD([[makeQuery(id+"F0.imprint","IMPRINT",EDGE,{"derivedFrom":sQuery(id+"F0.wireOp",EDGE,"E154")}),-1.0]])]});
            extrude(context, id + "F6", {"entities" : qUnion([Q0]), "depth" : 20 * mm, "offsetDistance" : 25 * mm});
        }
        {
            var Q0;
            Q0=makeQuery(id+"F6.opExtrude","SWEPT_FACE",FACE,{"disambiguationData":[OSD([sQuery(id+"F0.wireOp",EDGE,"E154")])]});
            extrude(context, id + "F7", {"entities" : qUnion([Q0]), "operationType" : NewBodyOperationType.ADD, "depth" : 25 * mm, "offsetDistance" : 25 * mm});
        }
        {
            var Q0;
            {var subQ0=sQuery(id+"F0.wireOp",EDGE,"E155");Q0=makeQuery(id+"F7.boolean.opBoolean","MERGE",FACE,{"derivedFrom":[makeQuery(id+"F6.opExtrude","SWEPT_FACE",FACE,{"disambiguationData":[OSD([subQ0])]}),makeQuery(id+"F7.opExtrude","SWEPT_FACE",FACE,{"disambiguationData":[OSD([sQuery(id+"F0.wireOp",EDGE,"E154"),subQ0])]})]});}
            extrude(context, id + "F8", {"entities" : qUnion([Q0]), "operationType" : NewBodyOperationType.ADD, "depth" : 10 * mm, "offsetDistance" : 25 * mm});
        }
        {
            var Q0;
            Q0=makeQuery(id+"F7.opExtrude","SWEPT_FACE",FACE,{"disambiguationData":[OSD([sQuery(id+"F0.wireOp",EDGE,"E154"),sQuery(id+"F0.wireOp",EDGE,"E175.filletArc")])]});
            extrude(context, id + "F9", {"entities" : qUnion([Q0]), "operationType" : NewBodyOperationType.ADD, "depth" : 10 * mm, "offsetDistance" : 25 * mm});
        }
        {
            var Q0;
            {var subQ0=sQuery(id+"F0.wireOp",EDGE,"E175.filletArc");var subQ1=sQuery(id+"F0.wireOp",EDGE,"E154");var subQ2=sQuery(id+"F0.wireOp",EDGE,"E155");Q0=makeQuery(id+"F9.boolean.opBoolean","MERGE",FACE,{"derivedFrom":[makeQuery(id+"F8.boolean.opBoolean","MERGE",FACE,{"derivedFrom":[makeQuery(id+"F7.boolean.opBoolean","MERGE",FACE,{"derivedFrom":[makeQuery(id+"F6.opExtrude","CAP_FACE",FACE,{"disambiguationData":[OSD([subQ1,subQ2,sQuery(id+"F0.wireOp",EDGE,"E156"),sQuery(id+"F0.wireOp",EDGE,"E157"),sQuery(id+"F0.wireOp",EDGE,"E158"),sQuery(id+"F0.wireOp",EDGE,"E159"),sQuery(id+"F0.wireOp",EDGE,"E160"),sQuery(id+"F0.wireOp",EDGE,"E161"),sQuery(id+"F0.wireOp",EDGE,"E162"),sQuery(id+"F0.wireOp",EDGE,"E163"),sQuery(id+"F0.wireOp",EDGE,"E164"),sQuery(id+"F0.wireOp",EDGE,"E165"),sQuery(id+"F0.wireOp",EDGE,"E166.filletArc"),sQuery(id+"F0.wireOp",EDGE,"E167.filletArc"),sQuery(id+"F0.wireOp",EDGE,"E168.filletArc"),sQuery(id+"F0.wireOp",EDGE,"E169.filletArc"),sQuery(id+"F0.wireOp",EDGE,"E170.filletArc"),sQuery(id+"F0.wireOp",EDGE,"E171.filletArc"),sQuery(id+"F0.wireOp",EDGE,"E172.filletArc"),sQuery(id+"F0.wireOp",EDGE,"E173.filletArc"),sQuery(id+"F0.wireOp",EDGE,"E174.filletArc"),subQ0,sQuery(id+"F0.wireOp",EDGE,"E176.filletArc")])],"isStart":true}),makeQuery(id+"F7.opExtrude","SWEPT_FACE",FACE,{"disambiguationData":[OSD([subQ1]),TDD([makeQuery(id+"F6.opExtrude","CAP_EDGE",EDGE,{"disambiguationData":[OSD([subQ1])],"isStart":true})])]})]}),makeQuery(id+"F8.opExtrude","SWEPT_FACE",FACE,{"disambiguationData":[OSD([subQ1,subQ2]),TDD([makeQuery(id+"F7.boolean.opBoolean","MERGE",EDGE,{"derivedFrom":[makeQuery(id+"F6.opExtrude","CAP_EDGE",EDGE,{"disambiguationData":[OSD([subQ2])],"isStart":true}),makeQuery(id+"F7.opExtrude","SWEPT_EDGE",EDGE,{"disambiguationData":[OSD([subQ1,subQ2]),TDD([makeQuery(id+"F6.opExtrude","CAP_VERTEX",VERTEX,{"disambiguationData":[OSD([subQ1,subQ2])],"isStart":true})])]})]})])]})]}),makeQuery(id+"F9.opExtrude","SWEPT_FACE",FACE,{"disambiguationData":[OSD([subQ1,subQ0]),TDD([makeQuery(id+"F7.opExtrude","SWEPT_EDGE",EDGE,{"disambiguationData":[OSD([subQ1,subQ0]),TDD([makeQuery(id+"F6.opExtrude","CAP_VERTEX",VERTEX,{"disambiguationData":[OSD([subQ1,subQ0])],"isStart":true})])]})])]})]});}
            var sketch = newSketch(context, id + "F10", { "sketchPlane" : qUnion([Q0])});
            skLineSegment(sketch, "E216.bottom", {"start": v(-68.27, 47.5) * mm, "end": v(-86.47, 47.5) * mm});
            skLineSegment(sketch, "E216.top", {"start": v(-68.27, 61.3) * mm, "end": v(-86.47, 61.3) * mm});
            skLineSegment(sketch, "E216.left", {"start": v(-66.27, 49.5) * mm, "end": v(-66.27, 59.3) * mm});
            skLineSegment(sketch, "E216.right", {"start": v(-88.47, 49.5) * mm, "end": v(-88.47, 59.3) * mm});
            skLineSegment(sketch, "E217", {"start": v(-61.27, 68.04) * mm, "end": v(-61.27, 16.26) * mm, "construction": true});
            skCircle(sketch, "E218", {"center": v(-61.27, 40.75) * mm, "radius": 2.05 * mm});
            skCircle(sketch, "E219", {"center": v(-61.27, 45.45) * mm, "radius": 1.45 * mm});
            skCircle(sketch, "E220", {"center": v(-61.27, 49.2) * mm, "radius": 1.1 * mm});
            skCircle(sketch, "E221", {"center": v(-61.27, 52.5) * mm, "radius": 1 * mm});
            skCircle(sketch, "E222", {"center": v(-61.27, 55.45) * mm, "radius": 0.75 * mm});
            skCircle(sketch, "E223", {"center": v(-61.27, 59.4) * mm, "radius": 2 * mm});
            skPoint(sketch, "E224.visualSharp", {"position": v(-88.47, 47.5) * mm});
            skArc(sketch, "E224.filletArc", {"start": v(-88.47, 49.5) * mm, "mid": v(-87.89, 48.1) * mm, "end": v(-86.47, 47.5) * mm});
            skPoint(sketch, "E225.visualSharp", {"position": v(-88.47, 61.3) * mm});
            skArc(sketch, "E225.filletArc", {"start": v(-86.47, 61.3) * mm, "mid": v(-87.89, 60.72) * mm, "end": v(-88.47, 59.3) * mm});
            skPoint(sketch, "E226.visualSharp", {"position": v(-66.27, 61.3) * mm});
            skArc(sketch, "E226.filletArc", {"start": v(-66.27, 59.3) * mm, "mid": v(-66.86, 60.72) * mm, "end": v(-68.27, 61.3) * mm});
            skPoint(sketch, "E227.visualSharp", {"position": v(-66.27, 47.5) * mm});
            skArc(sketch, "E227.filletArc", {"start": v(-68.27, 47.5) * mm, "mid": v(-66.86, 48.1) * mm, "end": v(-66.27, 49.5) * mm});
            skLineSegment(sketch, "E228", {"start": v(-95.27, 41.9) * mm, "end": v(-45.58, 41.9) * mm, "construction": true});
            skCircle(sketch, "E229", {"center": v(-86.17, 41.9) * mm, "radius": 2.5 * mm});
            skCircle(sketch, "E230", {"center": v(-79.97, 41.9) * mm, "radius": 2.5 * mm});
            skCircle(sketch, "E231", {"center": v(-73.77, 41.9) * mm, "radius": 2.5 * mm});
            skCircle(sketch, "E232", {"center": v(-67.57, 41.9) * mm, "radius": 2.5 * mm});
            skSolve(sketch);
        }
        {
            var Q0;
            Q0=makeQuery(id+"F10.imprint","IMPRINT",FACE,{"disambiguationData":[TD([[makeQuery(id+"F10.imprint","IMPRINT",EDGE,{"derivedFrom":sQuery(id+"F10.wireOp",EDGE,"E216.bottom")}),-1.0]])]});
            var Q1;
            Q1=makeQuery(id+"F10.imprint","IMPRINT",FACE,{"disambiguationData":[TD([[makeQuery(id+"F10.imprint","IMPRINT",EDGE,{"derivedFrom":sQuery(id+"F10.wireOp",EDGE,"E218")}),1.0]])]});
            var Q2;
            Q2=makeQuery(id+"F10.imprint","IMPRINT",FACE,{"disambiguationData":[TD([[makeQuery(id+"F10.imprint","IMPRINT",EDGE,{"derivedFrom":sQuery(id+"F10.wireOp",EDGE,"E219")}),1.0]])]});
            var Q3;
            Q3=makeQuery(id+"F10.imprint","IMPRINT",FACE,{"disambiguationData":[TD([[makeQuery(id+"F10.imprint","IMPRINT",EDGE,{"derivedFrom":sQuery(id+"F10.wireOp",EDGE,"E220")}),1.0]])]});
            var Q4;
            Q4=makeQuery(id+"F10.imprint","IMPRINT",FACE,{"disambiguationData":[TD([[makeQuery(id+"F10.imprint","IMPRINT",EDGE,{"derivedFrom":sQuery(id+"F10.wireOp",EDGE,"E221")}),1.0]])]});
            var Q5;
            Q5=makeQuery(id+"F10.imprint","IMPRINT",FACE,{"disambiguationData":[TD([[makeQuery(id+"F10.imprint","IMPRINT",EDGE,{"derivedFrom":sQuery(id+"F10.wireOp",EDGE,"E222")}),1.0]])]});
            var Q6;
            Q6=makeQuery(id+"F10.imprint","IMPRINT",FACE,{"disambiguationData":[TD([[makeQuery(id+"F10.imprint","IMPRINT",EDGE,{"derivedFrom":sQuery(id+"F10.wireOp",EDGE,"E223")}),1.0]])]});
            var Q7;
            Q7=makeQuery(id+"F10.imprint","IMPRINT",FACE,{"disambiguationData":[TD([[makeQuery(id+"F10.imprint","IMPRINT",EDGE,{"derivedFrom":sQuery(id+"F10.wireOp",EDGE,"E229")}),1.0]])]});
            var Q8;
            Q8=makeQuery(id+"F10.imprint","IMPRINT",FACE,{"disambiguationData":[TD([[makeQuery(id+"F10.imprint","IMPRINT",EDGE,{"derivedFrom":sQuery(id+"F10.wireOp",EDGE,"E230")}),1.0]])]});
            var Q9;
            Q9=makeQuery(id+"F10.imprint","IMPRINT",FACE,{"disambiguationData":[TD([[makeQuery(id+"F10.imprint","IMPRINT",EDGE,{"derivedFrom":sQuery(id+"F10.wireOp",EDGE,"E231")}),1.0]])]});
            var Q10;
            Q10=makeQuery(id+"F10.imprint","IMPRINT",FACE,{"disambiguationData":[TD([[makeQuery(id+"F10.imprint","IMPRINT",EDGE,{"derivedFrom":sQuery(id+"F10.wireOp",EDGE,"E232")}),1.0]])]});
            extrude(context, id + "F11", {"entities" : qUnion([Q0, Q1, Q2, Q3, Q4, Q5, Q6, Q7, Q8, Q9, Q10]), "operationType" : NewBodyOperationType.REMOVE, "endBound" : BoundingType.UP_TO_NEXT, "oppositeDirection" : true, "depth" : 25 * mm, "hasOffset" : true, "offsetDistance" : 2 * mm});
        }
        {
            var Q0;
            Q0=makeQuery(id+"F9.opExtrude","CAP_FACE",FACE,{"disambiguationData":[OSD([sQuery(id+"F0.wireOp",EDGE,"E154"),sQuery(id+"F0.wireOp",EDGE,"E175.filletArc")])],"isStart":false});
            var sketch = newSketch(context, id + "F12", { "sketchPlane" : qUnion([Q0])});
            skLineSegment(sketch, "E233.bottom", {"start": v(20, 37.5) * mm, "end": v(8, 37.5) * mm});
            skLineSegment(sketch, "E233.top", {"start": v(20, 62.5) * mm, "end": v(8, 62.5) * mm});
            skLineSegment(sketch, "E233.left", {"start": v(20, 37.5) * mm, "end": v(20, 62.5) * mm});
            skLineSegment(sketch, "E233.right", {"start": v(8, 37.5) * mm, "end": v(8, 62.5) * mm});
            skSolve(sketch);
        }
        {
            var Q0;
            Q0=makeQuery(id+"F12.imprint","IMPRINT",FACE,{"disambiguationData":[TD([[makeQuery(id+"F12.imprint","IMPRINT",EDGE,{"derivedFrom":sQuery(id+"F12.wireOp",EDGE,"E233.bottom")}),-1.0]])]});
            extrude(context, id + "F13", {"entities" : qUnion([Q0]), "operationType" : NewBodyOperationType.REMOVE, "oppositeDirection" : true, "depth" : 8 * mm, "offsetDistance" : 25 * mm});
        }
        {
            var Q0;
            {var subQ0=sQuery(id+"F0.wireOp",EDGE,"E155");var subQ1=sQuery(id+"F0.wireOp",EDGE,"E154");Q0=makeQuery(id+"F8.opExtrude","CAP_EDGE",EDGE,{"disambiguationData":[OSD([subQ1,subQ0]),TDD([makeQuery(id+"F7.opExtrude","CAP_EDGE",EDGE,{"disambiguationData":[OSD([subQ1,subQ0])],"isStart":false})])],"isStart":false});}
            var Q1;
            {var subQ0=sQuery(id+"F0.wireOp",EDGE,"E175.filletArc");var subQ1=sQuery(id+"F0.wireOp",EDGE,"E154");Q1=makeQuery(id+"F9.opExtrude","CAP_EDGE",EDGE,{"disambiguationData":[OSD([subQ1,subQ0]),TDD([makeQuery(id+"F7.opExtrude","CAP_EDGE",EDGE,{"disambiguationData":[OSD([subQ1,subQ0])],"isStart":false})])],"isStart":false});}
            var Q2;
            Q2=makeQuery(id+"F13.boolean.opBoolean","COPY",EDGE,{"derivedFrom":makeQuery(id+"F13.opExtrude","CAP_EDGE",EDGE,{"disambiguationData":[OSD([sQuery(id+"F12.wireOp",EDGE,"E233.top")])],"isStart":false})});
            var Q3;
            Q3=makeQuery(id+"F8.opExtrude","CAP_EDGE",EDGE,{"disambiguationData":[OSD([sQuery(id+"F0.wireOp",EDGE,"E155"),sQuery(id+"F0.wireOp",EDGE,"E174.filletArc")])],"isStart":false});
            var Q4;
            {var subQ0=sQuery(id+"F0.wireOp",EDGE,"E175.filletArc");var subQ1=sQuery(id+"F0.wireOp",EDGE,"E154");Q4=makeQuery(id+"F9.opExtrude","CAP_EDGE",EDGE,{"disambiguationData":[OSD([subQ1,subQ0]),TDD([makeQuery(id+"F7.boolean.opBoolean","MERGE",EDGE,{"derivedFrom":[makeQuery(id+"F6.opExtrude","SWEPT_EDGE",EDGE,{"disambiguationData":[OSD([subQ1,subQ0])]}),makeQuery(id+"F7.opExtrude","CAP_EDGE",EDGE,{"disambiguationData":[OSD([subQ1,subQ0])],"isStart":true})]})])],"isStart":false});}
            var Q5;
            Q5=makeQuery(id+"F13.boolean.opBoolean","COPY",EDGE,{"derivedFrom":makeQuery(id+"F13.opExtrude","CAP_EDGE",EDGE,{"disambiguationData":[OSD([sQuery(id+"F12.wireOp",EDGE,"E233.bottom")])],"isStart":false})});
            var Q6;
            Q6=makeQuery(id+"F13.boolean.opBoolean","COPY",EDGE,{"derivedFrom":makeQuery(id+"F13.opExtrude","CAP_EDGE",EDGE,{"disambiguationData":[OSD([sQuery(id+"F12.wireOp",EDGE,"E233.left")])],"isStart":false})});
            var Q7;
            {var subQ0=sQuery(id+"F0.wireOp",EDGE,"E175.filletArc");var subQ1=sQuery(id+"F0.wireOp",EDGE,"E154");var subQ2=sQuery(id+"F0.wireOp",EDGE,"E155");Q7=makeQuery(id+"F9.boolean.opBoolean","MERGE",EDGE,{"derivedFrom":[makeQuery(id+"F8.boolean.opBoolean","MERGE",EDGE,{"derivedFrom":[makeQuery(id+"F7.opExtrude","CAP_EDGE",EDGE,{"disambiguationData":[OSD([subQ1]),TDD([makeQuery(id+"F6.opExtrude","CAP_EDGE",EDGE,{"disambiguationData":[OSD([subQ1])],"isStart":false})])],"isStart":false}),makeQuery(id+"F8.opExtrude","SWEPT_EDGE",EDGE,{"disambiguationData":[OSD([subQ1,subQ2]),TDD([makeQuery(id+"F7.opExtrude","CAP_VERTEX",VERTEX,{"disambiguationData":[OSD([subQ1,subQ2]),TDD([makeQuery(id+"F6.opExtrude","CAP_VERTEX",VERTEX,{"disambiguationData":[OSD([subQ1,subQ2])],"isStart":false})])],"isStart":false})])]})]}),makeQuery(id+"F9.opExtrude","SWEPT_EDGE",EDGE,{"disambiguationData":[OSD([subQ1,subQ0]),TDD([makeQuery(id+"F7.opExtrude","CAP_VERTEX",VERTEX,{"disambiguationData":[OSD([subQ1,subQ0]),TDD([makeQuery(id+"F6.opExtrude","CAP_VERTEX",VERTEX,{"disambiguationData":[OSD([subQ1,subQ0])],"isStart":false})])],"isStart":false})])]})]});}
            var Q8;
            {var subQ0=sQuery(id+"F0.wireOp",EDGE,"E155");var subQ1=sQuery(id+"F0.wireOp",EDGE,"E154");Q8=makeQuery(id+"F8.opExtrude","CAP_EDGE",EDGE,{"disambiguationData":[OSD([subQ1,subQ0]),TDD([makeQuery(id+"F7.boolean.opBoolean","MERGE",EDGE,{"derivedFrom":[makeQuery(id+"F6.opExtrude","CAP_EDGE",EDGE,{"disambiguationData":[OSD([subQ0])],"isStart":false}),makeQuery(id+"F7.opExtrude","SWEPT_EDGE",EDGE,{"disambiguationData":[OSD([subQ1,subQ0]),TDD([makeQuery(id+"F6.opExtrude","CAP_VERTEX",VERTEX,{"disambiguationData":[OSD([subQ1,subQ0])],"isStart":false})])]})]})])],"isStart":false});}
            fillet(context, id + "F14", {"entities" : qUnion([Q0, Q1, Q2, Q3, Q4, Q5, Q6, Q7, Q8]), "radius" : 3 * mm, "tangentPropagation" : true, "allowEdgeOverflow" : false});
        }
        {
            var Q0;
            {var subQ0=sQuery(id+"F0.wireOp",EDGE,"E178");Q0=makeQuery(id+"F0.imprint","IMPRINT",FACE,{"disambiguationData":[TD([[makeQuery(id+"F0.imprint","IMPRINT",EDGE,{"derivedFrom":subQ0}),-1.0]])]});}
            var Q1;
            {var subQ0=sQuery(id+"F0.wireOp",EDGE,"E202");Q1=makeQuery(id+"F0.imprint","IMPRINT",FACE,{"disambiguationData":[TD([[makeQuery(id+"F0.imprint","IMPRINT",EDGE,{"derivedFrom":subQ0}),1.0]])]});}
            var Q2;
            {var subQ0=sQuery(id+"F0.wireOp",EDGE,"E207");Q2=makeQuery(id+"F0.imprint","IMPRINT",FACE,{"disambiguationData":[TD([[makeQuery(id+"F0.imprint","IMPRINT",EDGE,{"derivedFrom":subQ0}),-1.0]])]});}
            extrude(context, id + "F15", {"entities" : qUnion([Q0, Q1, Q2]), "depth" : 10 * mm, "offsetDistance" : 25 * mm});
        }
    });
